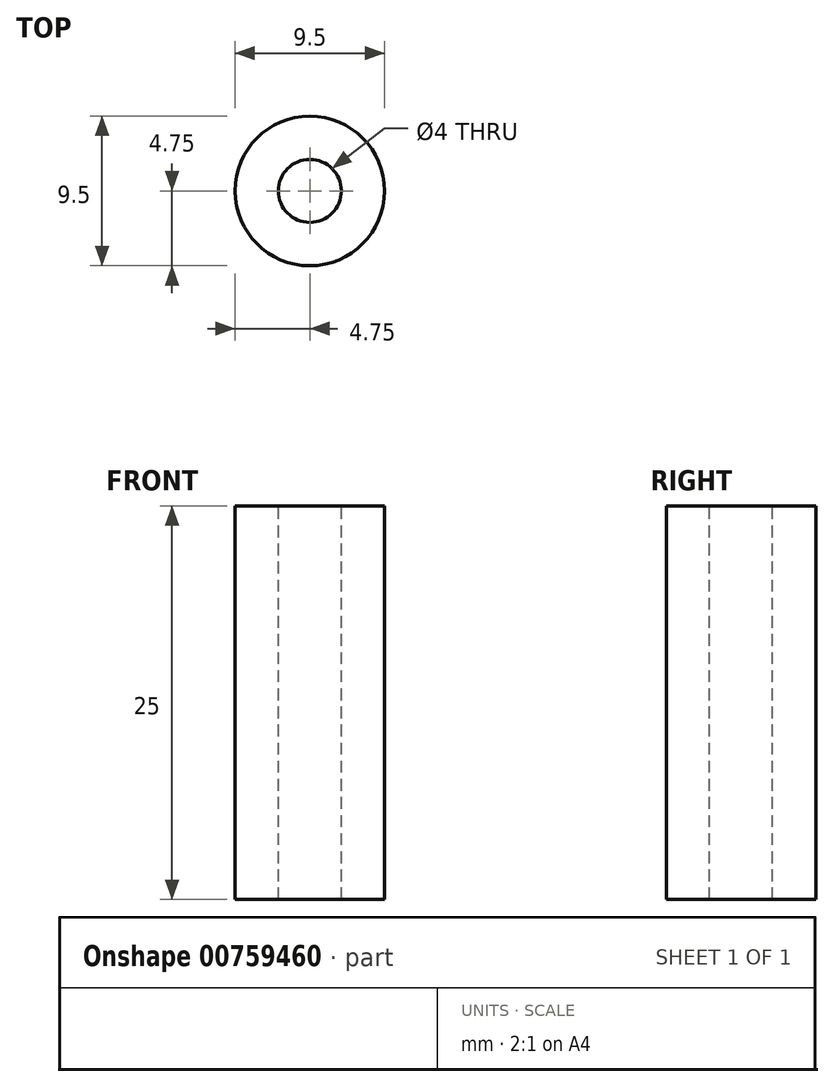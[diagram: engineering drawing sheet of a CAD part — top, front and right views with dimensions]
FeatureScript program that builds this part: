
annotation { "Feature Type Name" : "Feature", "Feature Type Description" : "" }
export const myFeature = defineFeature(function(context is Context, id is Id, definition is map)
    precondition{}
    {
        {
            var Q0;
            Q0=qCreatedBy(makeId("Top.planeOp"),FACE);
            var sketch = newSketch(context, id + "F0", { "sketchPlane" : qUnion([Q0])});
            skCircle(sketch, "E0", {"center": v(0, 0) * mm, "radius": 4.75 * mm});
            skCircle(sketch, "E1", {"center": v(0, 0) * mm, "radius": 2 * mm});
            skSolve(sketch);
        }
        {
            var Q0;
            Q0=makeQuery(id+"F0.imprint","IMPRINT",FACE,{"disambiguationData":[TD([[makeQuery(id+"F0.imprint","IMPRINT",EDGE,{"derivedFrom":sQuery(id+"F0.wireOp",EDGE,"E0")}),1.0]])]});
            extrude(context, id + "F1", {"entities" : qUnion([Q0]), "oppositeDirection" : true, "depth" : 25 * mm, "offsetDistance" : 25 * mm});
        }
    });
